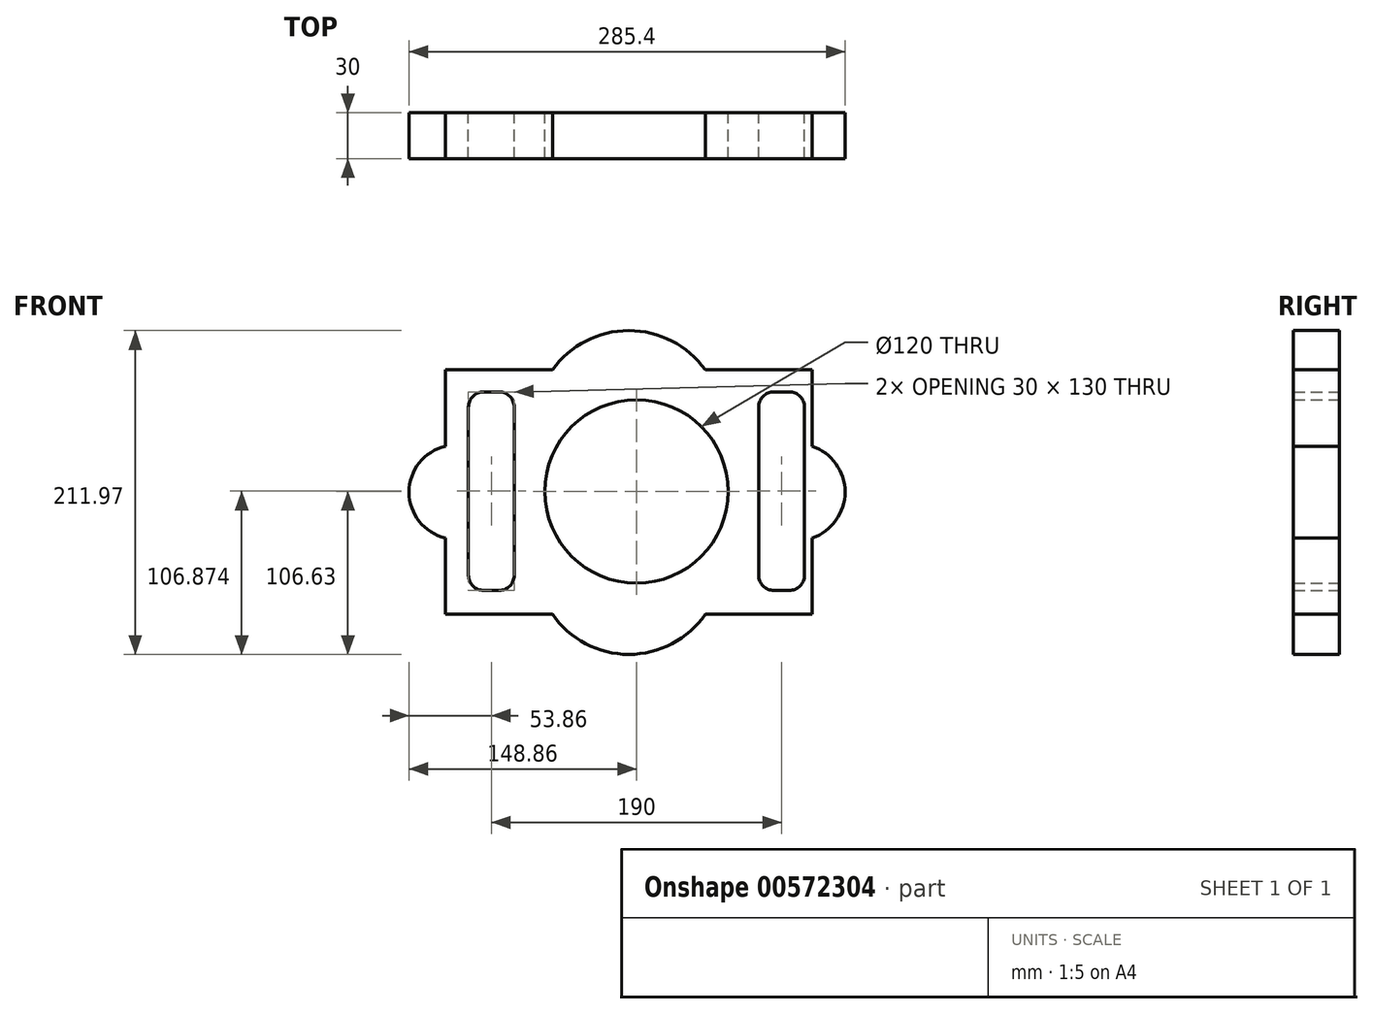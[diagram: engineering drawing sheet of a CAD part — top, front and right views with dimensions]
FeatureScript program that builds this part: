
annotation { "Feature Type Name" : "Feature", "Feature Type Description" : "" }
export const myFeature = defineFeature(function(context is Context, id is Id, definition is map)
    precondition{}
    {
        {
            var Q0;
            Q0=qCreatedBy(makeId("Front.planeOp"),FACE);
            var sketch = newSketch(context, id + "F0", { "sketchPlane" : qUnion([Q0])});
            skCircle(sketch, "E0", {"center": v(0, 0) * mm, "radius": 60 * mm});
            skLineSegment(sketch, "E1.bottom", {"start": v(-100, 65.24) * mm, "end": v(-90, 65.24) * mm});
            skLineSegment(sketch, "E1.top", {"start": v(-100, -64.76) * mm, "end": v(-90, -64.76) * mm});
            skLineSegment(sketch, "E1.left", {"start": v(-110, 55.24) * mm, "end": v(-110, -54.76) * mm});
            skLineSegment(sketch, "E1.right", {"start": v(-80, 55.24) * mm, "end": v(-80, -54.76) * mm});
            skLineSegment(sketch, "E2.bottom", {"start": v(90, 65.24) * mm, "end": v(100, 65.24) * mm});
            skLineSegment(sketch, "E2.top", {"start": v(90, -64.76) * mm, "end": v(100, -64.76) * mm});
            skLineSegment(sketch, "E2.left", {"start": v(80, 55.24) * mm, "end": v(80, -54.76) * mm});
            skLineSegment(sketch, "E2.right", {"start": v(110, 55.24) * mm, "end": v(110, -54.76) * mm});
            skPoint(sketch, "E3.visualSharp", {"position": v(-110, 65.24) * mm});
            skArc(sketch, "E3.filletArc", {"start": v(-100, 65.24) * mm, "mid": v(-107.07, 62.31) * mm, "end": v(-110, 55.24) * mm});
            skPoint(sketch, "E4.visualSharp", {"position": v(-80, 65.24) * mm});
            skArc(sketch, "E4.filletArc", {"start": v(-80, 55.24) * mm, "mid": v(-82.93, 62.31) * mm, "end": v(-90, 65.24) * mm});
            skPoint(sketch, "E5.visualSharp", {"position": v(-80, -64.76) * mm});
            skArc(sketch, "E5.filletArc", {"start": v(-90, -64.76) * mm, "mid": v(-82.93, -61.83) * mm, "end": v(-80, -54.76) * mm});
            skPoint(sketch, "E6.visualSharp", {"position": v(-110, -64.76) * mm});
            skArc(sketch, "E6.filletArc", {"start": v(-110, -54.76) * mm, "mid": v(-107.07, -61.83) * mm, "end": v(-100, -64.76) * mm});
            skPoint(sketch, "E7.visualSharp", {"position": v(80, -64.76) * mm});
            skArc(sketch, "E7.filletArc", {"start": v(80, -54.76) * mm, "mid": v(82.93, -61.83) * mm, "end": v(90, -64.76) * mm});
            skPoint(sketch, "E8.visualSharp", {"position": v(110, -64.76) * mm});
            skArc(sketch, "E8.filletArc", {"start": v(100, -64.76) * mm, "mid": v(107.07, -61.83) * mm, "end": v(110, -54.76) * mm});
            skPoint(sketch, "E9.visualSharp", {"position": v(110, 65.24) * mm});
            skArc(sketch, "E9.filletArc", {"start": v(110, 55.24) * mm, "mid": v(107.07, 62.31) * mm, "end": v(100, 65.24) * mm});
            skPoint(sketch, "E10.visualSharp", {"position": v(80, 65.24) * mm});
            skArc(sketch, "E10.filletArc", {"start": v(90, 65.24) * mm, "mid": v(82.93, 62.31) * mm, "end": v(80, 55.24) * mm});
            skLineSegment(sketch, "E11", {"start": v(-125, 79.6) * mm, "end": v(-125, 29.6) * mm});
            skLineSegment(sketch, "E12", {"start": v(-125, 29.6) * mm, "end": v(-125, -30.4) * mm});
            skLineSegment(sketch, "E13", {"start": v(-125, -30.4) * mm, "end": v(-125, -80.4) * mm});
            skLineSegment(sketch, "E14", {"start": v(-125, 79.6) * mm, "end": v(-55, 79.6) * mm});
            skLineSegment(sketch, "E15", {"start": v(-55, 79.6) * mm, "end": v(45, 79.6) * mm});
            skLineSegment(sketch, "E16", {"start": v(45, 79.6) * mm, "end": v(115, 79.6) * mm});
            skLineSegment(sketch, "E17", {"start": v(115, 79.6) * mm, "end": v(115, 29.6) * mm});
            skLineSegment(sketch, "E18", {"start": v(115, 29.6) * mm, "end": v(115, -30.4) * mm});
            skLineSegment(sketch, "E19", {"start": v(115, -30.4) * mm, "end": v(115, -80.4) * mm});
            skLineSegment(sketch, "E20", {"start": v(-125, -80.4) * mm, "end": v(-55, -80.4) * mm});
            skLineSegment(sketch, "E21", {"start": v(-55, -80.4) * mm, "end": v(45, -80.4) * mm});
            skLineSegment(sketch, "E22", {"start": v(45, -80.4) * mm, "end": v(115, -80.4) * mm});
            skArc(sketch, "E23", {"start": v(-125, 29.6) * mm, "mid": v(-148.86, -0.4) * mm, "end": v(-125, -30.4) * mm});
            skArc(sketch, "E24", {"start": v(115, -30.4) * mm, "mid": v(136.54, -0.4) * mm, "end": v(115, 29.6) * mm});
            skArc(sketch, "E25", {"start": v(45, 79.6) * mm, "mid": v(-5, 105.34) * mm, "end": v(-55, 79.6) * mm});
            skArc(sketch, "E26", {"start": v(-55, -80.4) * mm, "mid": v(-5, -106.63) * mm, "end": v(45, -80.4) * mm});
            skSolve(sketch);
        }
        {
            var Q0;
            Q0 = qSketchRegion(id + "F0", true);
            extrude(context, id + "F1", {"entities" : qUnion([Q0]), "depth" : 30 * mm, "offsetDistance" : 25 * mm});
        }
    });
